# Revit family: 28794XXX_new
name_source: partatom
category: Plumbing Fixtures
units: mm (PartAtom-declared; Revit-internal decimal feet)

## family parameters
Cut with Voids When Loaded = Yes
Host = Face
OmniClass Number = 23.31.17.00
OmniClass Title = Showers
Part Type = Normal
Room Calculation Point = No
Round Connector Dimension = Use Diameter
Shared = No

## types (1)
- Default - please load Revit Family Type Catalog
    Connector Description = Water Inlet 12.7mm
    Default Elevation = 1219 mm
    Description = AXOR Citterio C Overhead shower 270/270 1jet ceiling integrated
    Diameter = 13 mm
    Manufacturer = AXOR
    Material = AXOR - Metal - 000 Chrome
    Material 1 = AXOR - Plastic - Black
    Model = 28794XXX
    Product Guid = 1afc34eb-0ee4-441b-8280-f429eb2fbe3a
    Product Page URL = https://www.axor-design.com
    Product data url = https://bimobject.com
    URL = https://www.axor-design.com
    Version = 1

## geometry (parser evidence)
native form markers: Sweep x2
no freeform markers — native parametric forms only
